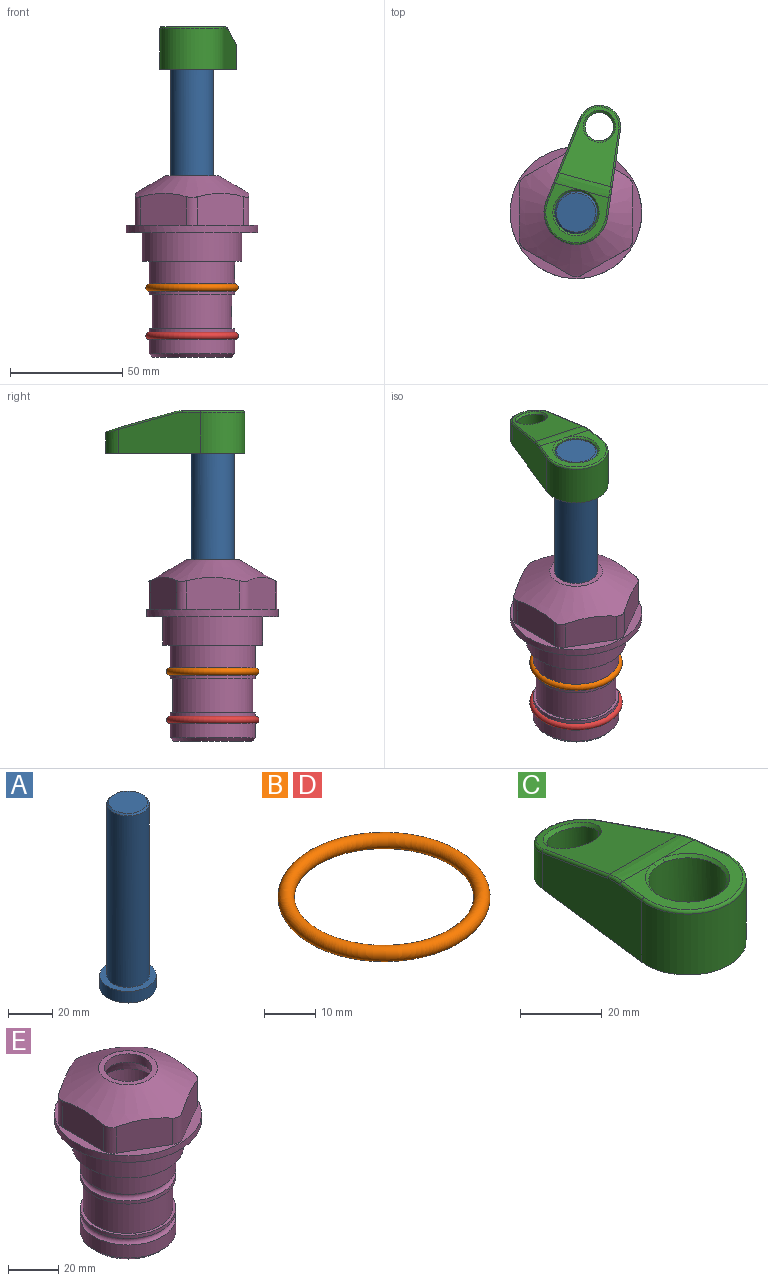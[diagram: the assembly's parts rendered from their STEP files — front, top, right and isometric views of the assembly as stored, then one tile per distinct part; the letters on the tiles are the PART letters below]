
ASSEMBLY  parts=5 mates=4
PART A: 6 faces, bbox 25.4x25.4x101.6 mm
  f0: plane 17.46x17.46mm, normal (0,0,1), area 239.5mm2, adj f5
  f1: plane 25.4x25.4mm, normal (0,0,-1), area 506.7mm2, adj f2
  f2: cylinder r=12.7mm len=25.4mm, axis (0,0,1), area 506.7mm2, adj f1,f3
  f3: plane 25.4x25.4mm, normal (0,0,1), area 221.7mm2, adj f2,f4
  f4: cylinder r=9.53mm len=94.46mm, axis (0,0,1), area 5653mm2, adj f3,f5
  f5: cone r=8.73mm half-angle=45deg, axis (0,0,-1), area 64.4mm2, adj f0,f4
PART B: 1 faces, bbox 44.7x44.7x3.2 mm
  f0: torus R=19.05mm, axis (0,0,1), area 1193.9mm2
PART C: 31 faces, bbox 31.7x65.5x19.8 mm
  f0: plane 39.12x18.26mm, normal (0.99,0.12,0), area 612.2mm2, adj f1,f4,f7,f11,f13,f15
  f1: cylinder r=9.53mm len=18.91mm, axis (0,0,-1), area 296.1mm2, adj f0,f2,f7,f17
  f2: plane 39.12x18.26mm, normal (-0.99,0.12,0), area 612.2mm2, adj f1,f4,f7,f12,f14,f16
  f3: cylinder r=6.35mm len=12.7mm, axis (0,0,-1), area 362.4mm2, adj f7,f18
  f4: cylinder r=14.29mm len=28.58mm, axis (0,0,-1), area 882.2mm2, adj f0,f2,f7,f10
  f5: cylinder r=9.53mm len=19.05mm, axis (0,0,-1), area 1092.6mm2, adj f7,f19,f20
  f6: plane 26.99x23.69mm, normal (0,0,1), area 216.2mm2, adj f9,f10,f11,f12,f19
  f7: plane 63.5x28.58mm, normal (0,0,-1), area 661.8mm2, adj f0,f1,f2,f3,f4,f5,f22,f23
  f8: plane 33.52x23.6mm, normal (0,0.26,0.97), area 486mm2, adj f9,f15,f16,f17,f18
  f9: cylinder r=19.05mm len=24.72mm, axis (1,0,0), area 120.4mm2, adj f6,f8,f13,f14,f20
  f10: torus R=13.49mm, axis (0,0,1), area 59mm2, adj f4,f6,f11,f12
  f11: cylinder r=0.79mm len=8.67mm, axis (0.12,-0.99,0), area 10.8mm2, adj f0,f6,f10,f13
  f12: cylinder r=0.79mm len=8.67mm, axis (0.12,0.99,0), area 10.8mm2, adj f2,f6,f10,f14
  f13: bspline ~4.95x1.42mm, area 6.1mm2, adj f0,f9,f11,f15
  f14: bspline ~4.95x1.42mm, area 6.1mm2, adj f2,f9,f12,f16
  f15: cylinder r=0.79mm len=25.95mm, axis (0.12,-0.96,0.26), area 32.9mm2, adj f0,f8,f13,f17
  f16: cylinder r=0.79mm len=25.95mm, axis (0.12,0.96,-0.26), area 32.9mm2, adj f2,f8,f14,f17
  f17: bspline ~18.91x8.38mm, area 30mm2, adj f1,f8,f15,f16
  f18: bspline ~14.29x14.29mm, area 48.3mm2, adj f3,f8
  f19: cone r=9.53mm half-angle=45deg, axis (0,0,1), area 66.5mm2, adj f5,f6,f20
  f20: bspline ~3.22x0.96mm, area 3.5mm2, adj f5,f9,f19
  f21: plane 2.75x2.72mm, normal (0,0,-1), area 2.9mm2, adj f23,f25,f28
  f22: plane 23.05x15.88mm, normal (-0.99,-0.12,0), area 323.6mm2, adj f7,f25,f26,f27,f28,f29
  f23: plane 23.05x15.88mm, normal (0.99,-0.12,0), area 323.6mm2, adj f7,f21,f25,f27,f28,f30
  f24: cylinder r=9.53mm len=10.69mm, axis (0,0,-1), area 114.7mm2, adj f7,f27,f29,f30
  f25: cylinder r=12.7mm len=20.59mm, axis (0,0,-1), area 381.1mm2, adj f7,f21,f22,f23,f26,f28
  f26: plane 2.75x2.72mm, normal (0,0,-1), area 2.9mm2, adj f22,f25,f28
  f27: plane 19.72x18.37mm, normal (0,-0.26,-0.97), area 291.8mm2, adj f22,f23,f24,f28,f29,f30
  f28: cylinder r=15.88mm len=19.92mm, axis (1,0,0), area 54.8mm2, adj f21,f22,f23,f25,f26,f27
  f29: cylinder r=1.59mm len=11mm, axis (0,0,-1), area 34.7mm2, adj f7,f22,f24,f27
  f30: cylinder r=1.59mm len=11mm, axis (0,0,-1), area 34.7mm2, adj f7,f23,f24,f27
PART D: same geometry as B
PART E: 36 faces, bbox 58.7x58.7x81 mm
  f0: cylinder r=17.78mm len=35.56mm, axis (0,0,1), area 1670.8mm2, adj f23,f24,f31
  f1: cylinder r=19.05mm len=38.1mm, axis (0,0,1), area 1191.9mm2, adj f26,f27,f30
  f2: plane 58.66x58.66mm, normal (0,0,-1), area 1150.6mm2, adj f3,f28
  f3: cylinder r=29.33mm len=58.66mm, axis (0,0,-1), area 585.1mm2, adj f2,f4
  f4: plane 58.66x58.66mm, normal (0,0,1), area 475.9mm2, adj f3,f5,f6,f7,f8,f9,f10,f11
  f5: plane 20.32x14.34mm, normal (-0.5,0.87,0), area 324.4mm2, adj f4,f15,f16,f17
  f6: plane 20.32x14.34mm, normal (0.5,0.87,0), area 324.4mm2, adj f4,f14,f15,f17
  f7: plane 23.48x14.34mm, normal (1,0,0), area 324.4mm2, adj f4,f13,f14,f17
  f8: plane 20.32x14.34mm, normal (0.5,-0.87,0), area 324.4mm2, adj f4,f12,f13,f17
  f9: plane 20.32x14.34mm, normal (-0.5,-0.87,0), area 324.4mm2, adj f4,f11,f12,f17
  f10: plane 23.48x14.34mm, normal (-1,0,0), area 324.4mm2, adj f4,f11,f16,f17
  f11: cylinder r=5.08mm len=12.85mm, axis (0,0,-1), area 67.2mm2, adj f4,f9,f10,f17
  f12: cylinder r=5.08mm len=12.85mm, axis (0,0,-1), area 67.2mm2, adj f4,f8,f9,f17
  f13: cylinder r=5.08mm len=12.85mm, axis (0,0,-1), area 67.2mm2, adj f4,f7,f8,f17
  f14: cylinder r=5.08mm len=12.85mm, axis (0,0,-1), area 67.2mm2, adj f4,f6,f7,f17
  f15: cylinder r=5.08mm len=12.85mm, axis (0,0,-1), area 67.2mm2, adj f4,f5,f6,f17
  f16: cylinder r=5.08mm len=12.85mm, axis (0,0,-1), area 67.2mm2, adj f4,f5,f10,f17
  f17: cone r=11.73mm half-angle=60deg, axis (0,0,-1), area 2071.8mm2, adj f5,f6,f7,f8,f9,f10,f11,f12
  f18: plane 23.46x23.46mm, normal (0,0,1), area 147.4mm2, adj f17,f35
  f19: plane 34.93x34.93mm, normal (0,0,-1), area 958mm2, adj f29
  f20: cylinder r=19.05mm len=38.1mm, axis (0,0,1), area 760.1mm2, adj f21,f29
  f21: torus R=19.05mm, axis (0,0,1), area 565.3mm2, adj f20,f22
  f22: cylinder r=19.05mm len=38.1mm, axis (0,0,1), area 190mm2, adj f21,f23
  f23: plane 38.1x38.1mm, normal (0,0,1), area 146.9mm2, adj f0,f22
  f24: plane 38.1x38.1mm, normal (0,0,-1), area 146.9mm2, adj f0,f25
  f25: cylinder r=19.05mm len=38.1mm, axis (0,0,1), area 190mm2, adj f24,f26
  f26: torus R=19.05mm, axis (0,0,1), area 565.3mm2, adj f1,f25
  f27: plane 44.45x44.45mm, normal (0,0,-1), area 411.7mm2, adj f1,f28
  f28: cylinder r=22.23mm len=44.45mm, axis (0,0,1), area 1773.5mm2, adj f2,f27
  f29: cone r=19.05mm half-angle=45deg, axis (0,0,1), area 257.5mm2, adj f19,f20
  f30: cylinder r=3.17mm len=6.75mm, axis (-1,0,0), area 128mm2, adj f1,f33
  f31: cylinder r=3.17mm len=6.35mm, axis (-1,0,0), area 102.5mm2, adj f0,f33
  f32: plane 25.4x25.4mm, normal (0,0,1), area 506.7mm2, adj f33
  f33: cylinder r=12.7mm len=66.42mm, axis (0,0,-1), area 5236.2mm2, adj f30,f31,f32,f34
  f34: cone r=9.53mm half-angle=30deg, axis (0,0,-1), area 443.4mm2, adj f33,f35
  f35: cylinder r=9.53mm len=19.05mm, axis (0,0,-1), area 240.9mm2, adj f18,f34
PLACE A rot(axis=(0,0,-1),15.2deg) t=(0,0,27.55)mm
PLACE B at identity
PLACE C rot(axis=(0,0,-1),15.2deg) t=(0,0,28.35)mm
PLACE D t=(0,0,-21.59)mm
PLACE E at identity fixed
MATE fastened C.f4 <-> A.f2  axis (0,0,-1) through (0,0,91.05)mm
MATE fastened D.f0 <-> E.f0  axis (0,0,1) through (0,0,-46.1)mm
MATE fastened E.f0 <-> B.f0  axis (0,0,1) through (0,0,-24.51)mm
MATE cylindrical A.f2 <-> E.f0  axis (0,0,-1) through (0,0,-10.55)mm
